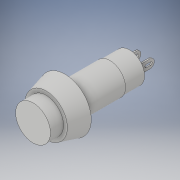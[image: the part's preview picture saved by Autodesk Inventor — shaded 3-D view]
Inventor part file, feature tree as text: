
AUTODESK INVENTOR PART (.ipt)
format: ipt  version: 2019 (Build 230136000, 136)  size: 170,496 bytes
history: native  units: mm
features: extrude x6, sketch x6, chamfer x1, fillet x1, projected_geometry x1
ambient origin geometry x8: Origin, YZ Plane, XZ Plane, XY Plane, X Axis, Y Axis, Z Axis, Center Point
bodies: Solid1 (feature_tree)
feature tree (15):
  extrude  "Extrusion1"  Depth=6.75mm TaperAngle=0.0deg
  extrude  "Extrusion2"  Depth=15.5mm TaperAngle=0.0deg
  extrude  "Extrusion3"  Depth=6.5mm TaperAngle=0.0deg
  chamfer  "Chamfer1"  Distance=6.5mm Angle=15.0deg
  extrude  "Extrusion4"  Depth=3.0mm
  fillet  "Fillet1"  Radius=0.5mm
  extrude  "Extrusion5"  Depth=5.1mm
  extrude  "Extrusion6"  Depth=4.5mm
  sketch  "Sketch1"  dims[d0=10.35mm d1=6.75mm d2=0.0mm]
  sketch  "Sketch2"  dims[d3=10.75mm d4=15.5mm d5=0.0mm]
  sketch  "Sketch3"  dims[d6=18.1mm d7=6.5mm d8=0.0mm d9=6.5mm d10=2.0mm d11=15.0deg]
  sketch  "Sketch4"  dims[d12=0.5mm d13=3.0mm d14=0.5mm]
  projected_geometry  "Projected Loop1"
  sketch  "Sketch5"  dims[d15=3.0mm d16=5.1mm]
  sketch  "Sketch6"  dims[d17=2.625mm d18=2.625mm d19=3.675mm d20=3.675mm d21=6.0mm d22=0.0mm d23=1.5mm d24=1.5mm d25=1.5mm d26=6.0mm d27=0.0mm d28=12.0mm d29=4.5mm d30=0.0mm]
